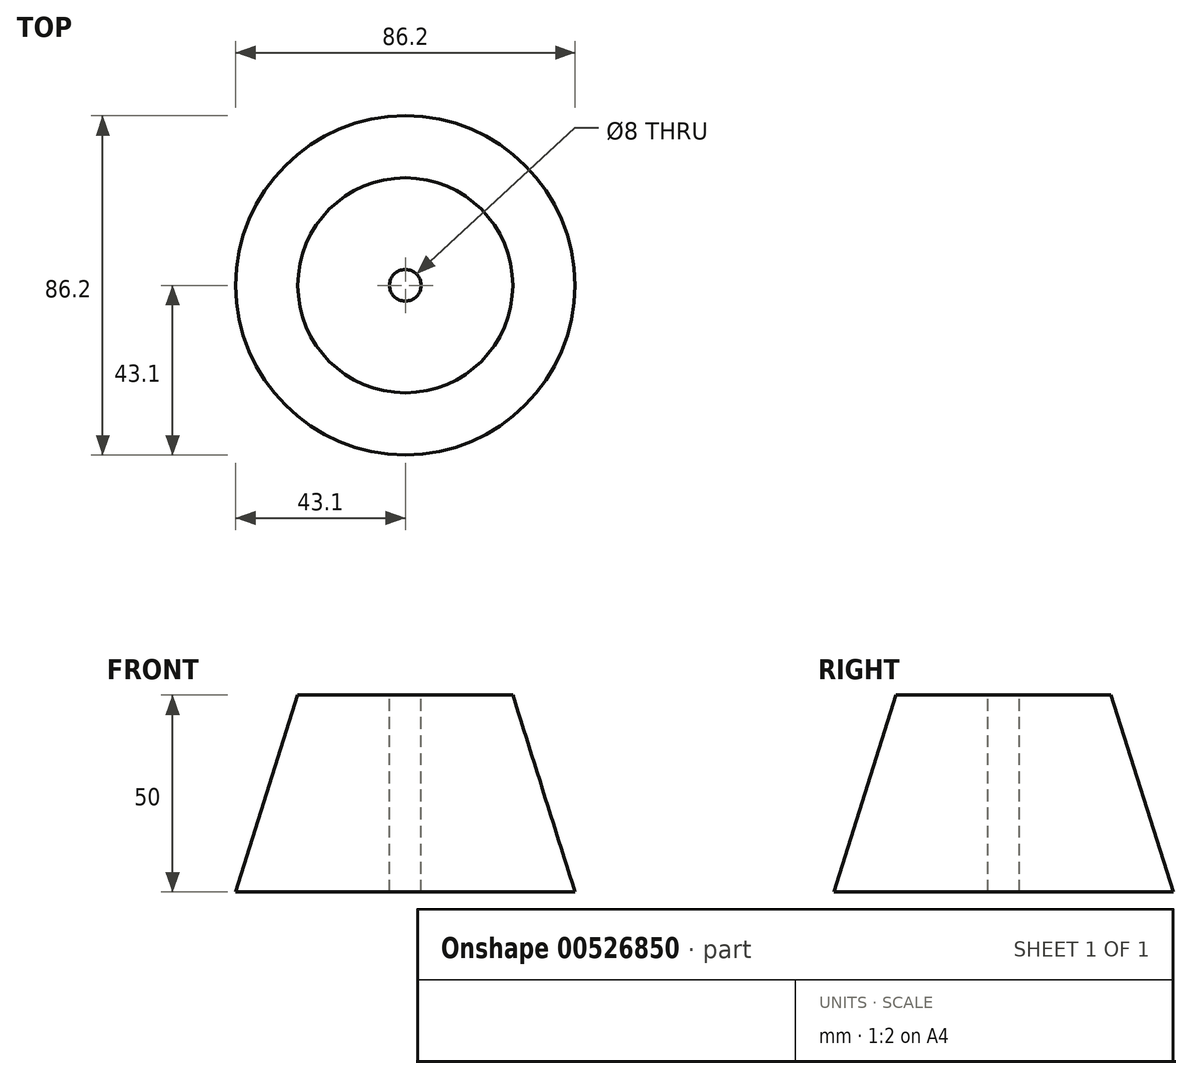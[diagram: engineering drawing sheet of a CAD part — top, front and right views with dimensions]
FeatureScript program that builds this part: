
annotation { "Feature Type Name" : "Feature", "Feature Type Description" : "" }
export const myFeature = defineFeature(function(context is Context, id is Id, definition is map)
    precondition{}
    {
        {
            var Q0;
            Q0=qCreatedBy(makeId("Front.planeOp"),FACE);
            var sketch = newSketch(context, id + "F0", { "sketchPlane" : qUnion([Q0])});
            skLineSegment(sketch, "E0", {"start": v(4, 40) * mm, "end": v(27.31, 40) * mm});
            skLineSegment(sketch, "E1", {"start": v(27.31, 40) * mm, "end": v(43.1, -10) * mm});
            skLineSegment(sketch, "E2", {"start": v(4, 40) * mm, "end": v(4, -10) * mm});
            skLineSegment(sketch, "E3", {"start": v(4, -10) * mm, "end": v(43.1, -10) * mm});
            skLineSegment(sketch, "E4", {"start": v(0, 69.17) * mm, "end": v(0, -52.93) * mm, "construction": true});
            skSolve(sketch);
        }
        {
            var Q0;
            Q0 = qSketchRegion(id + "F0", true);
            var Q1;
            Q1=sQuery(id+"F0.wireOp",EDGE,"E4");
            revolve(context, id + "F1", {"entities" : qUnion([Q0]), "axis" : qUnion([Q1]), "revolveType" : RevolveType.FULL});
        }
    });
